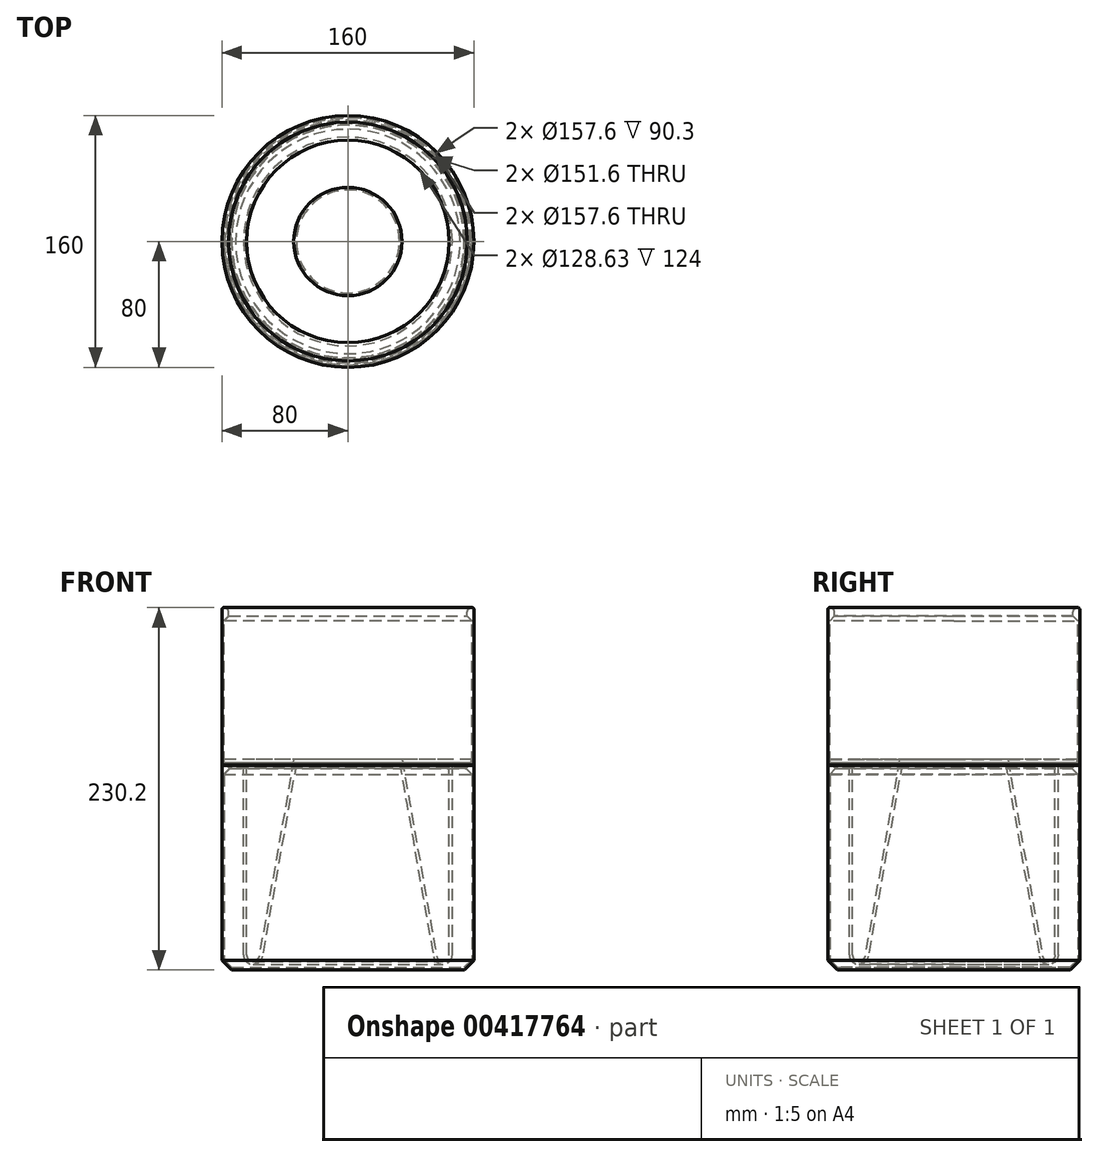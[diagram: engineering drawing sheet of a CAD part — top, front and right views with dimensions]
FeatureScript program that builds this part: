
annotation { "Feature Type Name" : "Feature", "Feature Type Description" : "" }
export const myFeature = defineFeature(function(context is Context, id is Id, definition is map)
    precondition{}
    {
        {
            var Q0;
            Q0=qCreatedBy(makeId("Front.planeOp"),FACE);
            var sketch = newSketch(context, id + "F0", { "sketchPlane" : qUnion([Q0])});
            skLineSegment(sketch, "E0", {"start": v(0, 0) * mm, "end": v(0, 1.5) * mm});
            skLineSegment(sketch, "E1", {"start": v(0, 1.5) * mm, "end": v(-78.8, 1.5) * mm});
            skLineSegment(sketch, "E2", {"start": v(-78.8, 1.5) * mm, "end": v(-78.8, 124.2) * mm});
            skLineSegment(sketch, "E3", {"start": v(-78.8, 124.2) * mm, "end": v(-75, 128) * mm});
            skLineSegment(sketch, "E4", {"start": v(-75, 128) * mm, "end": v(-77, 130) * mm});
            skLineSegment(sketch, "E5", {"start": v(-77, 130) * mm, "end": v(-80, 130) * mm});
            skLineSegment(sketch, "E6", {"start": v(-80, 130) * mm, "end": v(-80, 0) * mm});
            skLineSegment(sketch, "E7", {"start": v(-80, 0) * mm, "end": v(0, 0) * mm});
            skLineSegment(sketch, "E8", {"start": v(-75, 128) * mm, "end": v(0, 128) * mm, "construction": true});
            skSolve(sketch);
        }
        {
            var Q0;
            Q0=makeQuery(id+"F0.imprint","IMPRINT",FACE,{"disambiguationData":[TD([[makeQuery(id+"F0.imprint","IMPRINT",EDGE,{"derivedFrom":sQuery(id+"F0.wireOp",EDGE,"E0")}),1.0]])]});
            var Q1;
            Q1=sQuery(id+"F0.wireOp",EDGE,"E0");
            revolve(context, id + "F1", {"entities" : qUnion([Q0]), "axis" : qUnion([Q1]), "revolveType" : RevolveType.FULL});
        }
        {
            var Q0;
            Q0=makeQuery(id+"F1.opRevolve","SWEPT_EDGE",EDGE,{"disambiguationData":[OSD([sQuery(id+"F0.wireOp",EDGE,"E1"),sQuery(id+"F0.wireOp",EDGE,"E2")])]});
            chamfer(context, id + "F2", {"entities" : qUnion([Q0]), "width" : 5 * mm, "tangentPropagation" : true});
        }
        {
            var Q0;
            Q0=makeQuery(id+"F1.opRevolve","SWEPT_EDGE",EDGE,{"disambiguationData":[OSD([sQuery(id+"F0.wireOp",EDGE,"E6"),sQuery(id+"F0.wireOp",EDGE,"E7")])]});
            chamfer(context, id + "F3", {"entities" : qUnion([Q0]), "width" : 6 * mm, "tangentPropagation" : true});
        }
        {
            var Q0;
            Q0=qCreatedBy(makeId("Front.planeOp"),FACE);
            var sketch = newSketch(context, id + "F4", { "sketchPlane" : qUnion([Q0])});
            skLineSegment(sketch, "E9.0", {"start": v(80, 130) * mm, "end": v(-80, 130) * mm});
            skLineSegment(sketch, "E10", {"start": v(-85, 138) * mm, "end": v(-87, 140) * mm});
            skLineSegment(sketch, "E11", {"start": v(-80, 0) * mm, "end": v(-80, 150) * mm});
            skLineSegment(sketch, "E12", {"start": v(80, 150) * mm, "end": v(80, 0) * mm});
            skLineSegment(sketch, "E13", {"start": v(-68.8, 134.2) * mm, "end": v(-65, 138) * mm});
            skLineSegment(sketch, "E14", {"start": v(65, 138) * mm, "end": v(68.8, 134.2) * mm});
            skLineSegment(sketch, "E15.0", {"start": v(80, 130.2) * mm, "end": v(-80, 130.2) * mm});
            skLineSegment(sketch, "E16", {"start": v(-80, 130.2) * mm, "end": v(-80, 230.2) * mm});
            skLineSegment(sketch, "E17", {"start": v(-80, 230.2) * mm, "end": v(-75.8, 230.2) * mm});
            skLineSegment(sketch, "E18", {"start": v(-75.8, 230.2) * mm, "end": v(-75.8, 225.2) * mm});
            skLineSegment(sketch, "E19", {"start": v(-75.8, 225.2) * mm, "end": v(-78.8, 225.2) * mm});
            skLineSegment(sketch, "E20", {"start": v(-78.8, 225.2) * mm, "end": v(-78.8, 131.4) * mm});
            skLineSegment(sketch, "E21", {"start": v(-78.8, 131.4) * mm, "end": v(-78.4, 131.4) * mm});
            skLineSegment(sketch, "E22", {"start": v(0, 131.4) * mm, "end": v(0, 130.2) * mm});
            skLineSegment(sketch, "E23", {"start": v(0, 130.2) * mm, "end": v(-80, 130.2) * mm});
            skLineSegment(sketch, "E24", {"start": v(-77.2, 130.2) * mm, "end": v(-78.4, 131.4) * mm});
            skSolve(sketch);
        }
        {
            var Q0;
            {var subQ0=sQuery(id+"F4.wireOp",EDGE,"E16");Q0=makeQuery(id+"F4.imprint","IMPRINT",FACE,{"disambiguationData":[TD([[makeQuery(id+"F4.imprint","IMPRINT",EDGE,{"derivedFrom":subQ0}),-1.0]])]});}
            var Q1;
            Q1=sQuery(id+"F4.wireOp",EDGE,"E22");
            revolve(context, id + "F5", {"entities" : qUnion([Q0]), "axis" : qUnion([Q1]), "revolveType" : RevolveType.FULL});
        }
        {
            var Q0;
            Q0=makeQuery(id+"F5.opRevolve","SWEPT_EDGE",EDGE,{"disambiguationData":[OSD([sQuery(id+"F4.wireOp",EDGE,"E19"),sQuery(id+"F4.wireOp",EDGE,"E20")])]});
            chamfer(context, id + "F6", {"entities" : qUnion([Q0]), "width" : 3.5 * mm, "tangentPropagation" : true});
        }
        {
            var Q0;
            Q0=makeQuery(id+"F5.opRevolve","SWEPT_EDGE",EDGE,{"disambiguationData":[OSD([sQuery(id+"F4.wireOp",EDGE,"E17"),sQuery(id+"F4.wireOp",EDGE,"E18")])]});
            fillet(context, id + "F7", {"entities" : qUnion([Q0]), "radius" : 3 * mm, "tangentPropagation" : true, "allowEdgeOverflow" : false});
        }
        {
            var Q0;
            Q0=qCreatedBy(makeId("Front.planeOp"),FACE);
            var sketch = newSketch(context, id + "F8", { "sketchPlane" : qUnion([Q0])});
            skLineSegment(sketch, "E25", {"start": v(78.8, 245.2) * mm, "end": v(78.8, 151.4) * mm});
            skLineSegment(sketch, "E26", {"start": v(-78.8, 151.4) * mm, "end": v(-78.8, 245.2) * mm});
            skLineSegment(sketch, "E27.0.0", {"start": v(-78.8, 131.4) * mm, "end": v(78.8, 131.4) * mm});
            skLineSegment(sketch, "E28", {"start": v(88.4, 141.4) * mm, "end": v(87.2, 140.2) * mm});
            skLineSegment(sketch, "E29", {"start": v(-87.2, 140.2) * mm, "end": v(-88.4, 141.4) * mm});
            skLineSegment(sketch, "E30", {"start": v(87, 140) * mm, "end": v(85, 138) * mm});
            skLineSegment(sketch, "E31", {"start": v(-85, 138) * mm, "end": v(-87, 140) * mm});
            skLineSegment(sketch, "E32.0", {"start": v(-78.6, 131.6) * mm, "end": v(-78.32, 131.6) * mm});
            skLineSegment(sketch, "E33.0", {"start": v(-74.82, 128.1) * mm, "end": v(-78.32, 131.6) * mm});
            skLineSegment(sketch, "E34.0", {"start": v(-78.6, 131.6) * mm, "end": v(-78.6, 245.2) * mm});
            skLineSegment(sketch, "E35", {"start": v(-78.6, 133.6) * mm, "end": v(-64.32, 133.6) * mm});
            skLineSegment(sketch, "E36", {"start": v(0, 133.6) * mm, "end": v(0, 131.6) * mm});
            skLineSegment(sketch, "E37", {"start": v(-74.82, 128.1) * mm, "end": v(-71.32, 131.6) * mm});
            skLineSegment(sketch, "E38.trimOffspring", {"start": v(-71.32, 131.6) * mm, "end": v(-66.32, 131.6) * mm});
            skLineSegment(sketch, "E39", {"start": v(-66.32, 131.6) * mm, "end": v(-66.32, 9.6) * mm});
            skLineSegment(sketch, "E40", {"start": v(-54.4, 8.56) * mm, "end": v(-32.71, 131.6) * mm});
            skLineSegment(sketch, "E41", {"start": v(-64.32, 133.6) * mm, "end": v(-64.32, 9.6) * mm});
            skLineSegment(sketch, "E42", {"start": v(-56.38, 8.9) * mm, "end": v(-34.4, 133.6) * mm});
            skLineSegment(sketch, "E43", {"start": v(-64.32, 9.6) * mm, "end": v(-64.32, 133.6) * mm, "construction": true});
            skLineSegment(sketch, "E44.trimOffspring", {"start": v(-34.4, 133.6) * mm, "end": v(0, 133.6) * mm});
            skLineSegment(sketch, "E45.trimOffspring", {"start": v(-32.71, 131.6) * mm, "end": v(78.8, 131.6) * mm});
            skPoint(sketch, "E46.visualSharp", {"position": v(-64.32, -36.12) * mm});
            skArc(sketch, "E46.filletArc", {"start": v(-64.32, 9.6) * mm, "mid": v(-60.67, 5.62) * mm, "end": v(-56.38, 8.9) * mm});
            skArc(sketch, "E47.filletArc", {"start": v(-66.32, 9.6) * mm, "mid": v(-60.84, 3.62) * mm, "end": v(-54.4, 8.56) * mm});
            skSolve(sketch);
        }
        {
            var Q0;
            {var subQ1=sQuery(id+"F8.wireOp",EDGE,"E32.0");Q0=makeQuery(id+"F8.imprint","IMPRINT",FACE,{"disambiguationData":[TD([[makeQuery(id+"F8.imprint","IMPRINT",EDGE,{"derivedFrom":subQ1}),1.0]])]});}
            var Q1;
            {var subQ0=sQuery(id+"F8.wireOp",EDGE,"E33.0");var subQ1=sQuery(id+"F8.wireOp",EDGE,"E27.0.0");var subQ2=makeQuery(id+"F8.imprint","INTERSECT",VERTEX,{"derivedFrom":[subQ1,subQ0]});Q1=makeQuery(id+"F8.imprint","IMPRINT",FACE,{"disambiguationData":[TD([[makeQuery(id+"F8.imprint","IMPRINT",EDGE,{"disambiguationData":[TD([[subQ2,-1.0]])],"derivedFrom":subQ1}),-1.0]])]});}
            var Q2;
            {var subQ10=sQuery(id+"F8.wireOp",EDGE,"E46.filletArc");Q2=makeQuery(id+"F8.imprint","IMPRINT",FACE,{"disambiguationData":[TD([[makeQuery(id+"F8.imprint","IMPRINT",EDGE,{"derivedFrom":subQ10}),-1.0]])]});}
            var Q3;
            {var subQ4=sQuery(id+"F8.wireOp",EDGE,"E36");Q3=makeQuery(id+"F8.imprint","IMPRINT",FACE,{"disambiguationData":[TD([[makeQuery(id+"F8.imprint","IMPRINT",EDGE,{"derivedFrom":subQ4}),-1.0]])]});}
            var Q4;
            Q4=sQuery(id+"F8.wireOp",EDGE,"E36");
            revolve(context, id + "F9", {"entities" : qUnion([Q0, Q1, Q2, Q3]), "axis" : qUnion([Q4]), "revolveType" : RevolveType.FULL});
        }
        {
            var Q0;
            Q0=makeQuery(id+"F5.opRevolve","SWEPT_EDGE",EDGE,{"disambiguationData":[OSD([sQuery(id+"F4.wireOp",EDGE,"E16"),sQuery(id+"F4.wireOp",EDGE,"E17")])]});
            fillet(context, id + "F10", {"entities" : qUnion([Q0]), "radius" : 1.2 * mm, "tangentPropagation" : true, "allowEdgeOverflow" : false});
        }
    });
